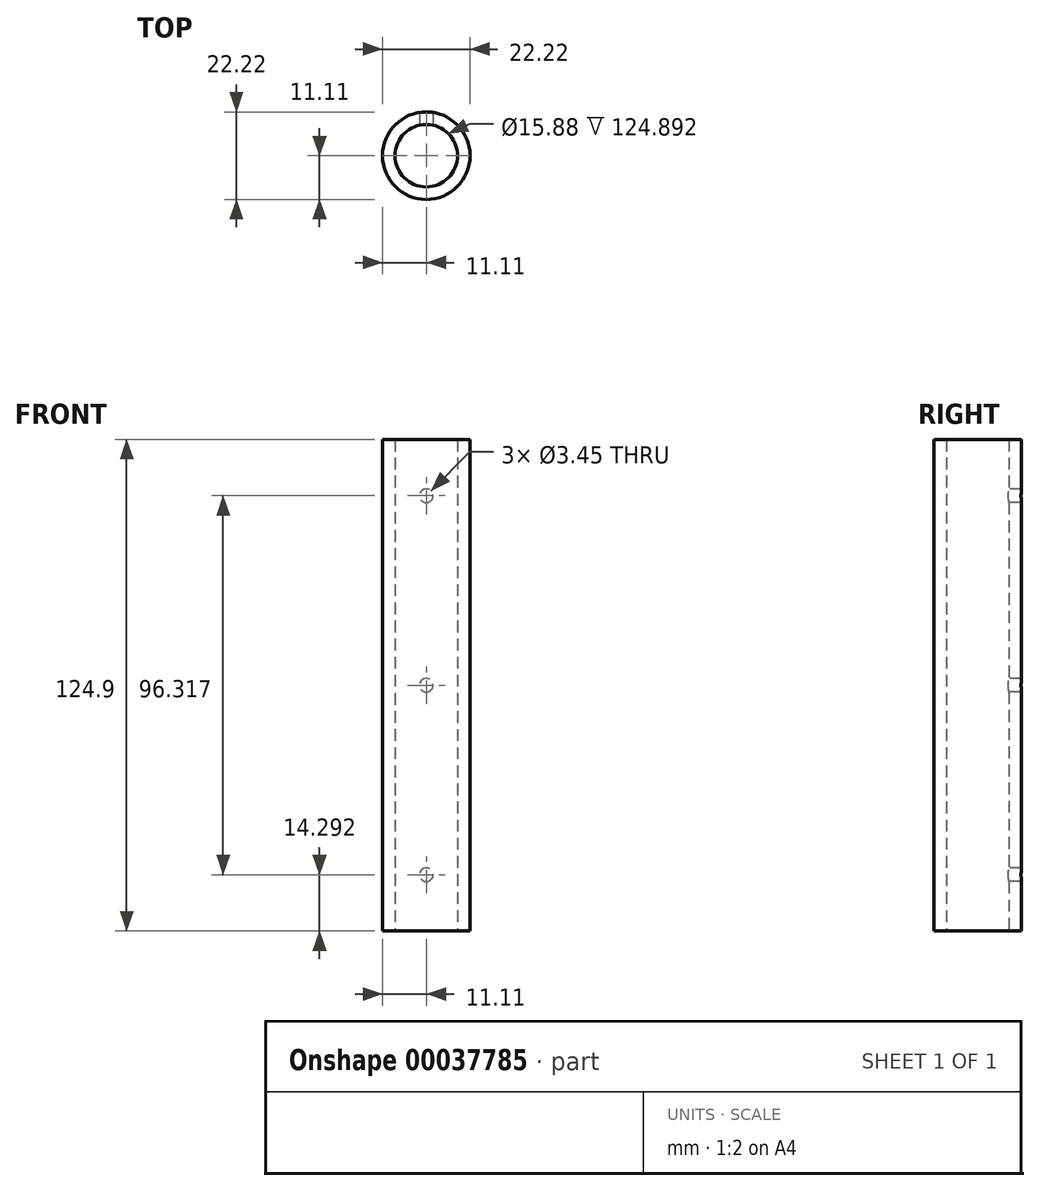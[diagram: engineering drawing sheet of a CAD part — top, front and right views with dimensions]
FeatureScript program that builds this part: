
annotation { "Feature Type Name" : "Feature", "Feature Type Description" : "" }
export const myFeature = defineFeature(function(context is Context, id is Id, definition is map)
    precondition{}
    {
        {
            var Q0;
            Q0=qCreatedBy(makeId("Top.planeOp"),FACE);
            var sketch = newSketch(context, id + "F0", { "sketchPlane" : qUnion([Q0])});
            skCircle(sketch, "E0", {"center": v(0, 0) * mm, "radius": 7.94 * mm});
            skCircle(sketch, "E1", {"center": v(0, 0) * mm, "radius": 11.11 * mm});
            skSolve(sketch);
        }
        {
            var Q0;
            Q0=qSketchRegion(id+"F0",true);
            extrude(context, id + "F1", {"entities" : qUnion([Q0]), "depth" : 67.74 * mm});
        }
        {
            var Q0;
            Q0=makeQuery(id+"F1.opExtrude","CAP_FACE",FACE,{"disambiguationData":[OSD([sQuery(id+"F0.wireOp",EDGE,"E0"),sQuery(id+"F0.wireOp",EDGE,"E1")])],"isStart":false});
            extrude(context, id + "F2", {"entities" : qUnion([Q0]), "operationType" : NewBodyOperationType.ADD, "depth" : 28.57 * mm});
        }
        {
            var Q0;
            Q0=makeQuery(id+"F1.opExtrude","CAP_FACE",FACE,{"disambiguationData":[OSD([sQuery(id+"F0.wireOp",EDGE,"E0"),sQuery(id+"F0.wireOp",EDGE,"E1")])],"isStart":true});
            extrude(context, id + "F3", {"entities" : qUnion([Q0]), "operationType" : NewBodyOperationType.ADD, "depth" : 28.57 * mm});
        }
        {
            var Q0;
            Q0=qCreatedBy(makeId("Front.planeOp"),FACE);
            var sketch = newSketch(context, id + "F4", { "sketchPlane" : qUnion([Q0])});
            skLineSegment(sketch, "E2", {"start": v(0, 67.74) * mm, "end": v(0, 0) * mm, "construction": true});
            skCircle(sketch, "E3", {"center": v(0, 33.87) * mm, "radius": 1.73 * mm});
            skLineSegment(sketch, "E4", {"start": v(0, 0) * mm, "end": v(0, -28.58) * mm, "construction": true});
            skLineSegment(sketch, "E5", {"start": v(0, 67.74) * mm, "end": v(0, 96.32) * mm, "construction": true});
            skCircle(sketch, "E6", {"center": v(0, 82.03) * mm, "radius": 1.73 * mm});
            skCircle(sketch, "E7", {"center": v(0, -14.29) * mm, "radius": 1.73 * mm});
            skSolve(sketch);
        }
        {
            var Q0;
            Q0 = qSketchRegion(id + "F4", true);
            var Q1;
            Q1=makeQuery(id+"F1.opExtrude","SWEPT_FACE",FACE,{"disambiguationData":[OSD([sQuery(id+"F0.wireOp",EDGE,"E1")])]});
            extrude(context, id + "F5", {"entities" : qUnion([Q0]), "operationType" : NewBodyOperationType.REMOVE, "endBound" : BoundingType.UP_TO_SURFACE, "oppositeDirection" : true, "endBoundEntityFace" : qUnion([Q1]), "depth" : 25.4 * mm});
        }
    });
